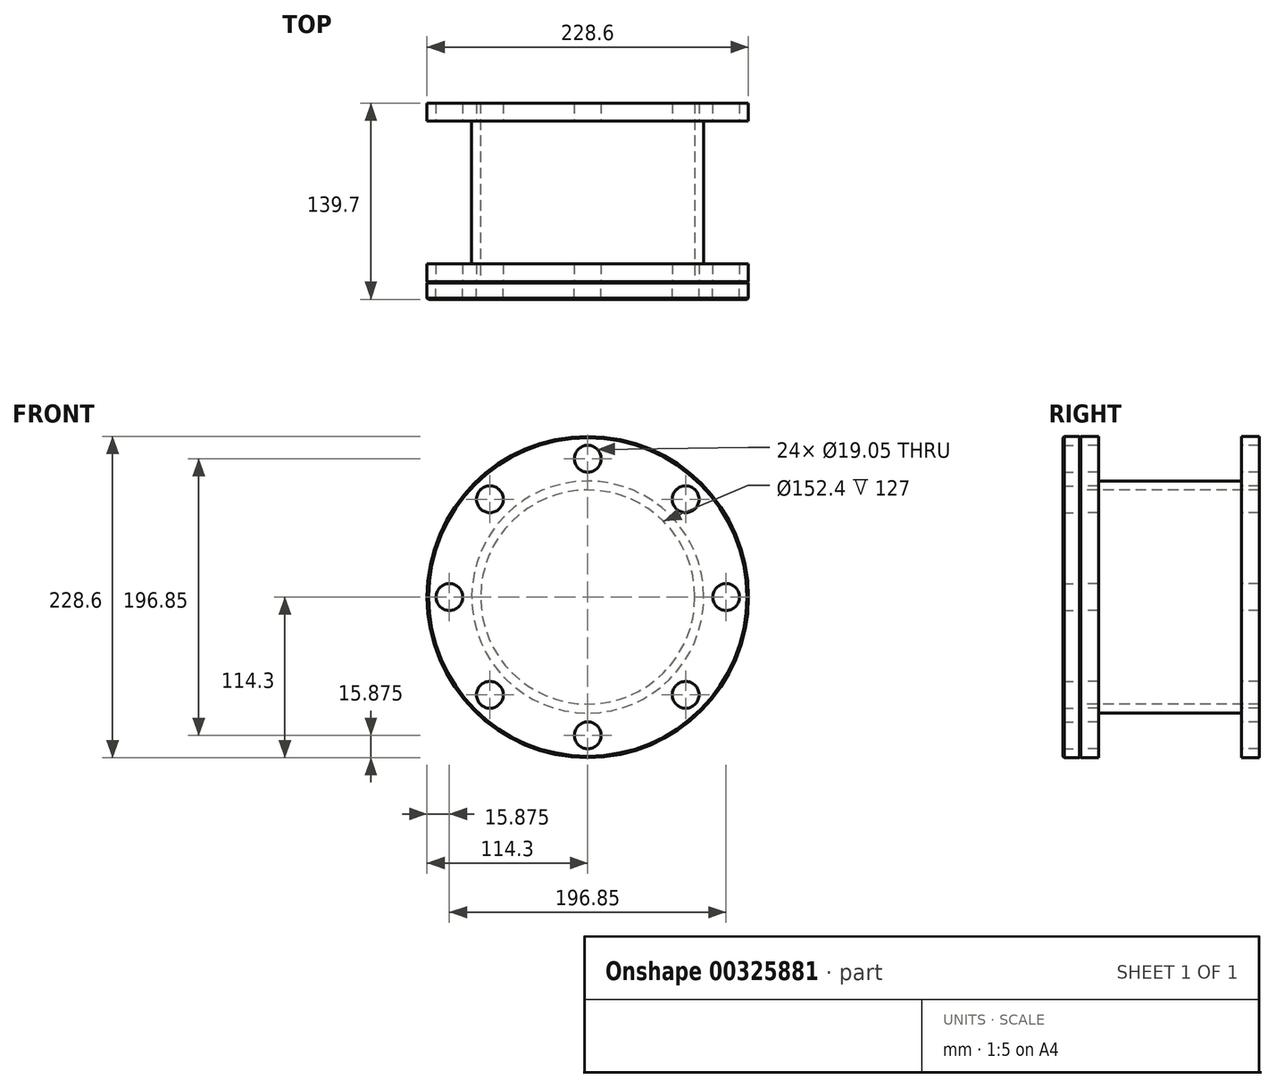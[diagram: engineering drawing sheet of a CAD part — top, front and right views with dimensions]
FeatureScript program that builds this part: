
annotation { "Feature Type Name" : "Feature", "Feature Type Description" : "" }
export const myFeature = defineFeature(function(context is Context, id is Id, definition is map)
    precondition{}
    {
        {
            var Q0;
            Q0=qCreatedBy(makeId("Right.planeOp"),FACE);
            var sketch = newSketch(context, id + "F0", { "sketchPlane" : qUnion([Q0])});
            skLineSegment(sketch, "E0", {"start": v(-372.41, 0) * mm, "end": v(512.39, 0) * mm, "construction": true});
            skLineSegment(sketch, "E1", {"start": v(0, 114.3) * mm, "end": v(-12.7, 114.3) * mm});
            skLineSegment(sketch, "E2", {"start": v(-12.7, 114.3) * mm, "end": v(-12.7, 82.55) * mm});
            skLineSegment(sketch, "E3", {"start": v(-12.7, 82.55) * mm, "end": v(-114.3, 82.55) * mm});
            skLineSegment(sketch, "E4", {"start": v(-114.3, 82.55) * mm, "end": v(-114.3, 114.3) * mm});
            skLineSegment(sketch, "E5", {"start": v(-114.3, 114.3) * mm, "end": v(-127, 114.3) * mm});
            skLineSegment(sketch, "E6", {"start": v(-127, 76.2) * mm, "end": v(0, 76.2) * mm});
            skLineSegment(sketch, "E7", {"start": v(-127, 114.3) * mm, "end": v(-127, 76.2) * mm});
            skLineSegment(sketch, "E8", {"start": v(0, 114.3) * mm, "end": v(0, 76.2) * mm});
            skSolve(sketch);
        }
        {
            var Q0;
            Q0=makeQuery(id+"F0.imprint","IMPRINT",FACE,{"disambiguationData":[TD([[makeQuery(id+"F0.imprint","IMPRINT",EDGE,{"derivedFrom":sQuery(id+"F0.wireOp",EDGE,"E1")}),1.0]])]});
            var Q1;
            Q1=sQuery(id+"F0.wireOp",EDGE,"E0");
            revolve(context, id + "F1", {"entities" : qUnion([Q0]), "axis" : qUnion([Q1]), "revolveType" : RevolveType.FULL});
        }
        {
            var Q0;
            Q0=makeQuery(id+"F1.opRevolve","SWEPT_FACE",FACE,{"disambiguationData":[OSD([sQuery(id+"F0.wireOp",EDGE,"E7")])]});
            cPlane(context, id + "F2", {"entities" : qUnion([Q0]), "cplaneType" : CPlaneType.OFFSET, "offset" : 0 * mm, "width" : 152.4 * mm, "height" : 152.4 * mm});
        }
        {
            var Q0;
            Q0=qCreatedBy(id+"F2.planeOp",FACE);
            var sketch = newSketch(context, id + "F3", { "sketchPlane" : qUnion([Q0])});
            skCircle(sketch, "E9", {"center": v(0, 0) * mm, "radius": 98.43 * mm, "construction": true});
            skCircle(sketch, "E10", {"center": v(0, 98.43) * mm, "radius": 9.53 * mm});
            skCircle(sketch, "E11.1.0", {"center": v(-69.6, 69.6) * mm, "radius": 9.53 * mm});
            skCircle(sketch, "E11.2.0", {"center": v(-98.43, 0) * mm, "radius": 9.53 * mm});
            skCircle(sketch, "E11.3.0", {"center": v(-69.6, -69.6) * mm, "radius": 9.53 * mm});
            skCircle(sketch, "E11.4.0", {"center": v(0, -98.43) * mm, "radius": 9.53 * mm});
            skCircle(sketch, "E11.5.0", {"center": v(69.6, -69.6) * mm, "radius": 9.53 * mm});
            skCircle(sketch, "E11.6.0", {"center": v(98.43, 0) * mm, "radius": 9.53 * mm});
            skCircle(sketch, "E11.7.0", {"center": v(69.6, 69.6) * mm, "radius": 9.53 * mm});
            skSolve(sketch);
        }
        {
            var Q0;
            Q0=qSketchRegion(id+"F3",true);
            extrude(context, id + "F4", {"entities" : qUnion([Q0]), "operationType" : NewBodyOperationType.REMOVE, "endBound" : BoundingType.THROUGH_ALL, "oppositeDirection" : true, "depth" : 635 * mm});
        }
        {
            var Q0;
            Q0=makeQuery(id+"F1.opRevolve","SWEPT_FACE",FACE,{"disambiguationData":[OSD([sQuery(id+"F0.wireOp",EDGE,"E7")])]});
            cPlane(context, id + "F5", {"entities" : qUnion([Q0]), "cplaneType" : CPlaneType.OFFSET, "offset" : 0 * mm, "width" : 152.4 * mm, "height" : 152.4 * mm});
        }
        {
            var Q0;
            Q0=qCreatedBy(id+"F5.planeOp",FACE);
            var sketch = newSketch(context, id + "F6", { "sketchPlane" : qUnion([Q0])});
            skCircle(sketch, "E12", {"center": v(0, 0) * mm, "radius": 98.43 * mm, "construction": true});
            skCircle(sketch, "E13", {"center": v(0, 98.43) * mm, "radius": 9.53 * mm});
            skCircle(sketch, "E14.1.0", {"center": v(-69.6, 69.6) * mm, "radius": 9.53 * mm});
            skCircle(sketch, "E14.2.0", {"center": v(-98.43, 0) * mm, "radius": 9.53 * mm});
            skCircle(sketch, "E14.3.0", {"center": v(-69.6, -69.6) * mm, "radius": 9.53 * mm});
            skCircle(sketch, "E14.4.0", {"center": v(0, -98.43) * mm, "radius": 9.53 * mm});
            skCircle(sketch, "E14.5.0", {"center": v(69.6, -69.6) * mm, "radius": 9.53 * mm});
            skCircle(sketch, "E14.6.0", {"center": v(98.42, 0) * mm, "radius": 9.53 * mm});
            skCircle(sketch, "E14.7.0", {"center": v(69.6, 69.6) * mm, "radius": 9.53 * mm});
            skCircle(sketch, "E15", {"center": v(0, 0) * mm, "radius": 114.3 * mm});
            skSolve(sketch);
        }
        {
            var Q0;
            Q0=makeQuery(id+"F6.imprint","IMPRINT",FACE,{"disambiguationData":[TD([[makeQuery(id+"F6.imprint","IMPRINT",EDGE,{"derivedFrom":sQuery(id+"F6.wireOp",EDGE,"E13")}),-1.0]])]});
            extrude(context, id + "F7", {"entities" : qUnion([Q0]), "depth" : 12.7 * mm});
        }
        {
            var Q0;
            Q0=makeQuery(id+"F7.opExtrude","SWEPT_FACE",FACE,{"disambiguationData":[OSD([sQuery(id+"F6.wireOp",EDGE,"E15")])]});
            chamfer(context, id + "F8", {"entities" : qUnion([Q0]), "width" : 1.02 * mm, "tangentPropagation" : true});
        }
    });
